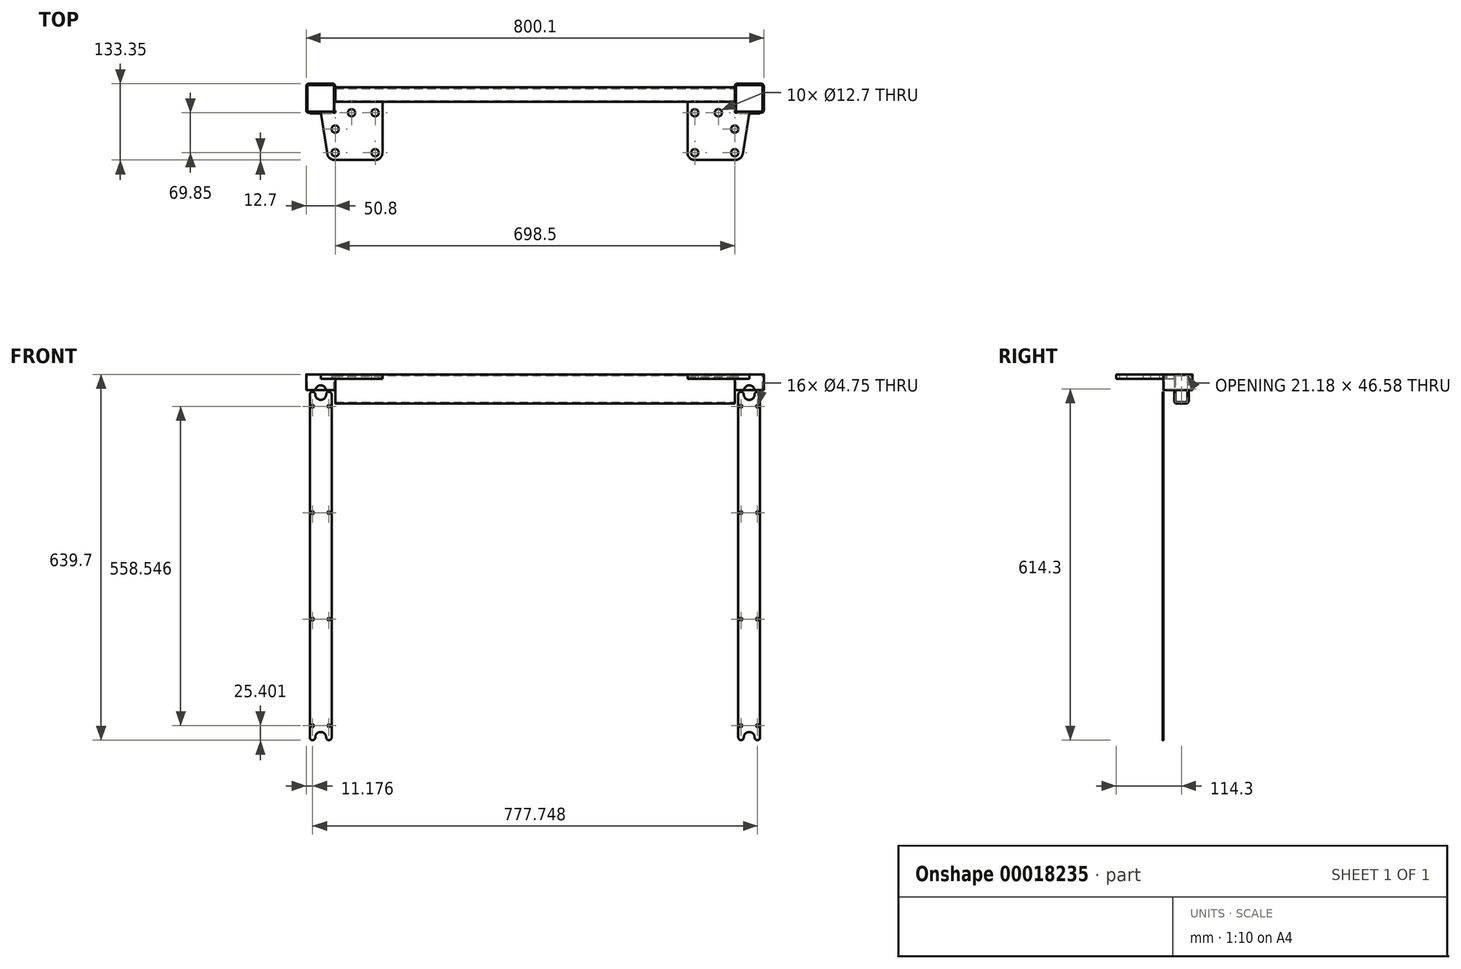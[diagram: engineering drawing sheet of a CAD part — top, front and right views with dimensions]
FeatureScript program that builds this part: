
annotation { "Feature Type Name" : "Feature", "Feature Type Description" : "" }
export const myFeature = defineFeature(function(context is Context, id is Id, definition is map)
    precondition{}
    {
        {
            var Q0;
            Q0=qCreatedBy(makeId("Top.planeOp"),FACE);
            var sketch = newSketch(context, id + "F0", { "sketchPlane" : qUnion([Q0])});
            skLineSegment(sketch, "E0.rect.bottom", {"start": v(-353.47, -25.4) * mm, "end": v(-395.83, -25.4) * mm});
            skLineSegment(sketch, "E0.rect.top", {"start": v(-353.47, 25.4) * mm, "end": v(-395.83, 25.4) * mm});
            skLineSegment(sketch, "E0.rect.left", {"start": v(-349.25, -21.18) * mm, "end": v(-349.25, 21.18) * mm});
            skLineSegment(sketch, "E0.rect.right", {"start": v(-400.05, -21.18) * mm, "end": v(-400.05, 21.18) * mm});
            skPoint(sketch, "E0.rect.middle", {"position": v(-374.65, 0) * mm});
            skLineSegment(sketch, "E1.0", {"start": v(-353.47, 23.3) * mm, "end": v(-395.83, 23.3) * mm});
            skLineSegment(sketch, "E1.1", {"start": v(-351.36, -21.18) * mm, "end": v(-351.36, 21.18) * mm});
            skLineSegment(sketch, "E1.2", {"start": v(-353.47, -23.3) * mm, "end": v(-395.83, -23.3) * mm});
            skLineSegment(sketch, "E1.3", {"start": v(-397.94, -21.18) * mm, "end": v(-397.94, 21.18) * mm});
            skPoint(sketch, "E2.visualSharp", {"position": v(-400.05, 25.4) * mm});
            skArc(sketch, "E2.filletArc", {"start": v(-395.83, 25.4) * mm, "mid": v(-398.82, 24.17) * mm, "end": v(-400.05, 21.18) * mm});
            skPoint(sketch, "E3.visualSharp", {"position": v(-349.25, 25.4) * mm});
            skArc(sketch, "E3.filletArc", {"start": v(-349.25, 21.18) * mm, "mid": v(-350.48, 24.17) * mm, "end": v(-353.47, 25.4) * mm});
            skPoint(sketch, "E4.visualSharp", {"position": v(-349.25, -25.4) * mm});
            skArc(sketch, "E4.filletArc", {"start": v(-353.47, -25.4) * mm, "mid": v(-350.48, -24.17) * mm, "end": v(-349.25, -21.18) * mm});
            skPoint(sketch, "E5.visualSharp", {"position": v(-400.05, -25.4) * mm});
            skArc(sketch, "E5.filletArc", {"start": v(-400.05, -21.18) * mm, "mid": v(-398.82, -24.17) * mm, "end": v(-395.83, -25.4) * mm});
            skPoint(sketch, "E6.visualSharp", {"position": v(-397.94, -23.3) * mm});
            skArc(sketch, "E6.filletArc", {"start": v(-397.94, -21.18) * mm, "mid": v(-397.32, -22.67) * mm, "end": v(-395.83, -23.3) * mm});
            skPoint(sketch, "E7.visualSharp", {"position": v(-351.36, -23.3) * mm});
            skArc(sketch, "E7.filletArc", {"start": v(-353.47, -23.3) * mm, "mid": v(-351.98, -22.67) * mm, "end": v(-351.36, -21.18) * mm});
            skPoint(sketch, "E8.visualSharp", {"position": v(-351.36, 23.3) * mm});
            skArc(sketch, "E8.filletArc", {"start": v(-351.36, 21.18) * mm, "mid": v(-351.98, 22.67) * mm, "end": v(-353.47, 23.3) * mm});
            skPoint(sketch, "E9.visualSharp", {"position": v(-397.94, 23.3) * mm});
            skArc(sketch, "E9.filletArc", {"start": v(-395.83, 23.3) * mm, "mid": v(-397.32, 22.67) * mm, "end": v(-397.94, 21.18) * mm});
            skLineSegment(sketch, "E10", {"start": v(0, 0) * mm, "end": v(0, 97.6) * mm, "construction": true});
            skSolve(sketch);
        }
        {
            assignVariable(context, id + "F1", {"name" : "A", "anyValue" : 27.62});
        }
        {
            var Q0;
            Q0=makeQuery(id+"F0.imprint","IMPRINT",FACE,{"disambiguationData":[TD([[makeQuery(id+"F0.imprint","IMPRINT",EDGE,{"derivedFrom":sQuery(id+"F0.wireOp",EDGE,"E0.rect.bottom")}),-1.0]])]});
            extrude(context, id + "F2", {"entities" : qUnion([Q0]), "oppositeDirection" : true, "depth" : (getVariable(context, 'A')) * mm});
        }
        {
            var Q0;
            Q0=makeQuery(id+"F2.opExtrude","SWEPT_FACE",FACE,{"disambiguationData":[OSD([sQuery(id+"F0.wireOp",EDGE,"E0.rect.left")])]});
            var sketch = newSketch(context, id + "F3", { "sketchPlane" : qUnion([Q0])});
            skLineSegment(sketch, "E11.bottom", {"start": v(-2.13, 0) * mm, "end": v(14.83, 0) * mm});
            skLineSegment(sketch, "E11.top", {"start": v(-2.13, -50.8) * mm, "end": v(14.83, -50.8) * mm});
            skLineSegment(sketch, "E11.left", {"start": v(-6.35, -4.22) * mm, "end": v(-6.35, -46.58) * mm});
            skLineSegment(sketch, "E11.right", {"start": v(19.05, -4.22) * mm, "end": v(19.05, -46.58) * mm});
            skPoint(sketch, "E12.visualSharp", {"position": v(-6.35, 0) * mm});
            skArc(sketch, "E12.filletArc", {"start": v(-2.13, 0) * mm, "mid": v(-5.12, -1.23) * mm, "end": v(-6.35, -4.22) * mm});
            skPoint(sketch, "E13.visualSharp", {"position": v(-6.35, -50.8) * mm});
            skArc(sketch, "E13.filletArc", {"start": v(-6.35, -46.58) * mm, "mid": v(-5.12, -49.57) * mm, "end": v(-2.13, -50.8) * mm});
            skPoint(sketch, "E14.visualSharp", {"position": v(19.05, -50.8) * mm});
            skArc(sketch, "E14.filletArc", {"start": v(14.83, -50.8) * mm, "mid": v(17.82, -49.57) * mm, "end": v(19.05, -46.58) * mm});
            skPoint(sketch, "E15.visualSharp", {"position": v(19.05, 0) * mm});
            skArc(sketch, "E15.filletArc", {"start": v(19.05, -4.22) * mm, "mid": v(17.82, -1.23) * mm, "end": v(14.83, 0) * mm});
            skLineSegment(sketch, "E16.0", {"start": v(16.94, -4.22) * mm, "end": v(16.94, -46.58) * mm});
            skLineSegment(sketch, "E16.1", {"start": v(-2.13, -2.1) * mm, "end": v(14.83, -2.1) * mm});
            skLineSegment(sketch, "E16.2", {"start": v(-4.24, -4.22) * mm, "end": v(-4.24, -46.58) * mm});
            skLineSegment(sketch, "E16.3", {"start": v(-2.13, -48.7) * mm, "end": v(14.83, -48.7) * mm});
            skPoint(sketch, "E17.visualSharp", {"position": v(16.94, -2.1) * mm});
            skArc(sketch, "E17.filletArc", {"start": v(16.94, -4.22) * mm, "mid": v(16.32, -2.73) * mm, "end": v(14.83, -2.1) * mm});
            skPoint(sketch, "E18.visualSharp", {"position": v(-4.24, -2.1) * mm});
            skArc(sketch, "E18.filletArc", {"start": v(-2.13, -2.1) * mm, "mid": v(-3.62, -2.73) * mm, "end": v(-4.24, -4.22) * mm});
            skPoint(sketch, "E19.visualSharp", {"position": v(-4.24, -48.7) * mm});
            skArc(sketch, "E19.filletArc", {"start": v(-4.24, -46.58) * mm, "mid": v(-3.62, -48.07) * mm, "end": v(-2.13, -48.7) * mm});
            skPoint(sketch, "E20.visualSharp", {"position": v(16.94, -48.7) * mm});
            skArc(sketch, "E20.filletArc", {"start": v(14.83, -48.7) * mm, "mid": v(16.32, -48.07) * mm, "end": v(16.94, -46.58) * mm});
            skSolve(sketch);
        }
        {
            var Q0;
            Q0 = qSketchRegion(id + "F3", true);
            var Q1;
            Q1=qCreatedBy(makeId("Right.planeOp"),FACE);
            extrude(context, id + "F4", {"entities" : qUnion([Q0]), "endBound" : BoundingType.UP_TO_SURFACE, "endBoundEntityFace" : qUnion([Q1]), "depth" : 25.4 * mm});
        }
        {
            var Q0;
            Q0=makeQuery(id+"F2.opExtrude","CAP_FACE",FACE,{"disambiguationData":[OSD([sQuery(id+"F0.wireOp",EDGE,"E0.rect.bottom"),sQuery(id+"F0.wireOp",EDGE,"E0.rect.top"),sQuery(id+"F0.wireOp",EDGE,"E0.rect.left"),sQuery(id+"F0.wireOp",EDGE,"E0.rect.right"),sQuery(id+"F0.wireOp",EDGE,"E1.0"),sQuery(id+"F0.wireOp",EDGE,"E1.1"),sQuery(id+"F0.wireOp",EDGE,"E1.2"),sQuery(id+"F0.wireOp",EDGE,"E1.3"),sQuery(id+"F0.wireOp",EDGE,"E2.filletArc"),sQuery(id+"F0.wireOp",EDGE,"E3.filletArc"),sQuery(id+"F0.wireOp",EDGE,"E4.filletArc"),sQuery(id+"F0.wireOp",EDGE,"E5.filletArc"),sQuery(id+"F0.wireOp",EDGE,"E6.filletArc"),sQuery(id+"F0.wireOp",EDGE,"E7.filletArc"),sQuery(id+"F0.wireOp",EDGE,"E8.filletArc"),sQuery(id+"F0.wireOp",EDGE,"E9.filletArc")])],"isStart":true});
            var sketch = newSketch(context, id + "F5", { "sketchPlane" : qUnion([Q0])});
            skLineSegment(sketch, "E21", {"start": v(-266.7, -6.35) * mm, "end": v(-266.7, -95.25) * mm});
            skCircle(sketch, "E22.MirrorC", {"center": v(-349.25, -95.25) * mm, "radius": 6.35 * mm});
            skLineSegment(sketch, "E23.MirrorCS", {"start": v(-374.65, -25.4) * mm, "end": v(-349.25, -25.4) * mm});
            skLineSegment(sketch, "E24.MirrorCS", {"start": v(-374.65, -25.4) * mm, "end": v(-363.2, -97.25) * mm});
            skArc(sketch, "E25.MirrorCS", {"start": v(-350.67, -107.95) * mm, "mid": v(-358.91, -104.91) * mm, "end": v(-363.2, -97.25) * mm});
            skLineSegment(sketch, "E26.MirrorCS", {"start": v(-279.4, -107.95) * mm, "end": v(-350.67, -107.95) * mm});
            skCircle(sketch, "E27.MirrorC", {"center": v(-320.68, -25.4) * mm, "radius": 6.35 * mm});
            skLineSegment(sketch, "E28.MirrorCS", {"start": v(-266.7, -6.35) * mm, "end": v(-349.25, -6.35) * mm});
            skLineSegment(sketch, "E29.MirrorCS", {"start": v(-349.25, -6.35) * mm, "end": v(-349.25, -25.4) * mm});
            skCircle(sketch, "E30.MirrorC", {"center": v(-279.4, -25.4) * mm, "radius": 6.35 * mm});
            skCircle(sketch, "E31.MirrorC", {"center": v(-279.4, -95.25) * mm, "radius": 6.35 * mm});
            skArc(sketch, "E32.MirrorCS", {"start": v(-266.7, -95.25) * mm, "mid": v(-270.42, -104.23) * mm, "end": v(-279.4, -107.95) * mm});
            skCircle(sketch, "E33.MirrorC", {"center": v(-349.25, -53.97) * mm, "radius": 6.35 * mm});
            skSolve(sketch);
        }
        {
            var Q0;
            Q0 = qSketchRegion(id + "F5", true);
            extrude(context, id + "F6", {"entities" : qUnion([Q0]), "oppositeDirection" : true, "depth" : 7.94 * mm});
        }
        {
            var Q0;
            Q0=makeQuery(id+"F4.opExtrude","SWEPT_BODY",BODY,{"disambiguationData":[OSD([sQuery(id+"F3.wireOp",EDGE,"E11.bottom"),sQuery(id+"F3.wireOp",EDGE,"E11.top"),sQuery(id+"F3.wireOp",EDGE,"E11.left"),sQuery(id+"F3.wireOp",EDGE,"E11.right"),sQuery(id+"F3.wireOp",EDGE,"E12.filletArc"),sQuery(id+"F3.wireOp",EDGE,"E13.filletArc"),sQuery(id+"F3.wireOp",EDGE,"E14.filletArc"),sQuery(id+"F3.wireOp",EDGE,"E15.filletArc"),sQuery(id+"F3.wireOp",EDGE,"E16.0"),sQuery(id+"F3.wireOp",EDGE,"E16.1"),sQuery(id+"F3.wireOp",EDGE,"E16.2"),sQuery(id+"F3.wireOp",EDGE,"E16.3"),sQuery(id+"F3.wireOp",EDGE,"E17.filletArc"),sQuery(id+"F3.wireOp",EDGE,"E18.filletArc"),sQuery(id+"F3.wireOp",EDGE,"E19.filletArc"),sQuery(id+"F3.wireOp",EDGE,"E20.filletArc")])]});
            var Q1;
            Q1=qCreatedBy(makeId("Right.planeOp"),FACE);
            mirror(context, id + "F7", {"operationType" : NewBodyOperationType.ADD, "entities" : qUnion([Q0]), "mirrorPlane" : qUnion([Q1])});
        }
        {
            var Q0;
            Q0=makeQuery(id+"F2.opExtrude","SWEPT_FACE",FACE,{"disambiguationData":[OSD([sQuery(id+"F0.wireOp",EDGE,"E0.rect.bottom")])]});
            var sketch = newSketch(context, id + "F8", { "sketchPlane" : qUnion([Q0])});
            skLineSegment(sketch, "E34.left", {"start": v(-384.18, -28.58) * mm, "end": v(-384.18, -641.35) * mm});
            skLineSegment(sketch, "E34.right", {"start": v(-365.13, -28.58) * mm, "end": v(-365.13, -641.35) * mm});
            skArc(sketch, "E35", {"start": v(-384.18, -641.35) * mm, "mid": v(-374.65, -650.88) * mm, "end": v(-365.13, -641.35) * mm});
            skArc(sketch, "E36", {"start": v(-365.13, -28.58) * mm, "mid": v(-374.65, -19.05) * mm, "end": v(-384.18, -28.58) * mm});
            skCircle(sketch, "E37", {"center": v(-388.87, -614.3) * mm, "radius": 1.85 * mm});
            skCircle(sketch, "E38.0.1.0", {"center": v(-388.87, -428.12) * mm, "radius": 1.85 * mm});
            skCircle(sketch, "E38.0.2.0", {"center": v(-388.87, -241.94) * mm, "radius": 1.85 * mm});
            skCircle(sketch, "E38.0.3.0", {"center": v(-388.87, -55.75) * mm, "radius": 1.85 * mm});
            skCircle(sketch, "E38.1.0.0", {"center": v(-360.3, -614.3) * mm, "radius": 1.85 * mm});
            skCircle(sketch, "E38.1.1.0", {"center": v(-360.3, -428.12) * mm, "radius": 1.85 * mm});
            skCircle(sketch, "E38.1.2.0", {"center": v(-360.3, -241.94) * mm, "radius": 1.85 * mm});
            skCircle(sketch, "E38.1.3.0", {"center": v(-360.3, -55.75) * mm, "radius": 1.85 * mm});
            skLineSegment(sketch, "E38.direction1", {"start": v(-388.87, -614.3) * mm, "end": v(-360.3, -614.3) * mm, "construction": true});
            skLineSegment(sketch, "E38.direction2", {"start": v(-388.87, -614.3) * mm, "end": v(-388.87, -428.12) * mm, "construction": true});
            skSolve(sketch);
        }
        {
            var Q0;
            Q0 = qSketchRegion(id + "F8", true);
            extrude(context, id + "F9", {"entities" : qUnion([Q0]), "operationType" : NewBodyOperationType.REMOVE, "oppositeDirection" : true, "depth" : 25.4 * mm});
        }
        {
            var Q0;
            Q0=makeQuery(id+"F6.opExtrude","SWEPT_BODY",BODY,{"disambiguationData":[OSD([sQuery(id+"F5.wireOp",EDGE,"E21"),sQuery(id+"F5.wireOp",EDGE,"E22.MirrorC"),sQuery(id+"F5.wireOp",EDGE,"E23.MirrorCS"),sQuery(id+"F5.wireOp",EDGE,"E24.MirrorCS"),sQuery(id+"F5.wireOp",EDGE,"E25.MirrorCS"),sQuery(id+"F5.wireOp",EDGE,"E26.MirrorCS"),sQuery(id+"F5.wireOp",EDGE,"E27.MirrorC"),sQuery(id+"F5.wireOp",EDGE,"E28.MirrorCS"),sQuery(id+"F5.wireOp",EDGE,"E29.MirrorCS"),sQuery(id+"F5.wireOp",EDGE,"E30.MirrorC"),sQuery(id+"F5.wireOp",EDGE,"E31.MirrorC"),sQuery(id+"F5.wireOp",EDGE,"E32.MirrorCS"),sQuery(id+"F5.wireOp",EDGE,"E33.MirrorC")])]});
            var Q1;
            Q1=makeQuery(id+"F2.opExtrude","SWEPT_BODY",BODY,{"disambiguationData":[OSD([sQuery(id+"F0.wireOp",EDGE,"E0.rect.bottom"),sQuery(id+"F0.wireOp",EDGE,"E0.rect.top"),sQuery(id+"F0.wireOp",EDGE,"E0.rect.left"),sQuery(id+"F0.wireOp",EDGE,"E0.rect.right"),sQuery(id+"F0.wireOp",EDGE,"E1.0"),sQuery(id+"F0.wireOp",EDGE,"E1.1"),sQuery(id+"F0.wireOp",EDGE,"E1.2"),sQuery(id+"F0.wireOp",EDGE,"E1.3"),sQuery(id+"F0.wireOp",EDGE,"E2.filletArc"),sQuery(id+"F0.wireOp",EDGE,"E3.filletArc"),sQuery(id+"F0.wireOp",EDGE,"E4.filletArc"),sQuery(id+"F0.wireOp",EDGE,"E5.filletArc"),sQuery(id+"F0.wireOp",EDGE,"E6.filletArc"),sQuery(id+"F0.wireOp",EDGE,"E7.filletArc"),sQuery(id+"F0.wireOp",EDGE,"E8.filletArc"),sQuery(id+"F0.wireOp",EDGE,"E9.filletArc")])]});
            var Q2;
            Q2=qCreatedBy(makeId("Right.planeOp"),FACE);
            mirror(context, id + "F10", {"entities" : qUnion([Q0, Q1]), "mirrorPlane" : qUnion([Q2])});
        }
        {
            var Q0;
            Q0=makeQuery(id+"F2.opExtrude","SWEPT_FACE",FACE,{"disambiguationData":[OSD([sQuery(id+"F0.wireOp",EDGE,"E0.rect.bottom")])]});
            var sketch = newSketch(context, id + "F11", { "sketchPlane" : qUnion([Q0])});
            skCircle(sketch, "E39", {"center": v(-388.87, -614.3) * mm, "radius": 2.37 * mm});
            skArc(sketch, "E40", {"start": v(-393.64, -634.94) * mm, "mid": v(-388.88, -639.7) * mm, "end": v(-384.11, -634.94) * mm});
            skLineSegment(sketch, "E41", {"start": v(-393.64, -634.94) * mm, "end": v(-393.64, -35.11) * mm});
            skLineSegment(sketch, "E42", {"start": v(-355.54, -35.12) * mm, "end": v(-355.54, -634.94) * mm});
            skArc(sketch, "E43", {"start": v(-365.06, -634.94) * mm, "mid": v(-360.3, -639.7) * mm, "end": v(-355.54, -634.94) * mm});
            skArc(sketch, "E44", {"start": v(-365.06, -634.94) * mm, "mid": v(-374.59, -625.42) * mm, "end": v(-384.11, -634.94) * mm});
            skArc(sketch, "E45", {"start": v(-384.11, -35.11) * mm, "mid": v(-388.87, -30.35) * mm, "end": v(-393.64, -35.11) * mm});
            skArc(sketch, "E46", {"start": v(-384.11, -35.11) * mm, "mid": v(-374.59, -44.64) * mm, "end": v(-365.06, -35.12) * mm});
            skArc(sketch, "E47", {"start": v(-355.54, -35.12) * mm, "mid": v(-360.3, -30.36) * mm, "end": v(-365.06, -35.12) * mm});
            skCircle(sketch, "E48", {"center": v(-388.87, -55.75) * mm, "radius": 2.37 * mm});
            skCircle(sketch, "E49", {"center": v(-360.3, -55.75) * mm, "radius": 2.37 * mm});
            skCircle(sketch, "E50", {"center": v(-360.3, -614.3) * mm, "radius": 2.37 * mm});
            skCircle(sketch, "E51", {"center": v(-388.87, -428.12) * mm, "radius": 2.37 * mm});
            skCircle(sketch, "E52", {"center": v(-360.3, -428.12) * mm, "radius": 2.37 * mm});
            skCircle(sketch, "E53", {"center": v(-388.87, -241.94) * mm, "radius": 2.37 * mm});
            skCircle(sketch, "E54", {"center": v(-360.3, -241.94) * mm, "radius": 2.37 * mm});
            skSolve(sketch);
        }
        {
            var Q0;
            Q0 = qSketchRegion(id + "F11", true);
            extrude(context, id + "F12", {"entities" : qUnion([Q0]), "depth" : 1.21 * mm});
        }
        {
            var Q0;
            Q0=makeQuery(id+"F12.opExtrude","SWEPT_BODY",BODY,{"disambiguationData":[OSD([sQuery(id+"F11.wireOp",EDGE,"E39"),sQuery(id+"F11.wireOp",EDGE,"E40"),sQuery(id+"F11.wireOp",EDGE,"E41"),sQuery(id+"F11.wireOp",EDGE,"E42"),sQuery(id+"F11.wireOp",EDGE,"E43"),sQuery(id+"F11.wireOp",EDGE,"E44"),sQuery(id+"F11.wireOp",EDGE,"E45"),sQuery(id+"F11.wireOp",EDGE,"E46"),sQuery(id+"F11.wireOp",EDGE,"E47"),sQuery(id+"F11.wireOp",EDGE,"E48"),sQuery(id+"F11.wireOp",EDGE,"E49"),sQuery(id+"F11.wireOp",EDGE,"E50"),sQuery(id+"F11.wireOp",EDGE,"E51"),sQuery(id+"F11.wireOp",EDGE,"E52"),sQuery(id+"F11.wireOp",EDGE,"E53"),sQuery(id+"F11.wireOp",EDGE,"E54")])]});
            var Q1;
            Q1=qCreatedBy(makeId("Right.planeOp"),FACE);
            mirror(context, id + "F13", {"entities" : qUnion([Q0]), "mirrorPlane" : qUnion([Q1])});
        }
    });
